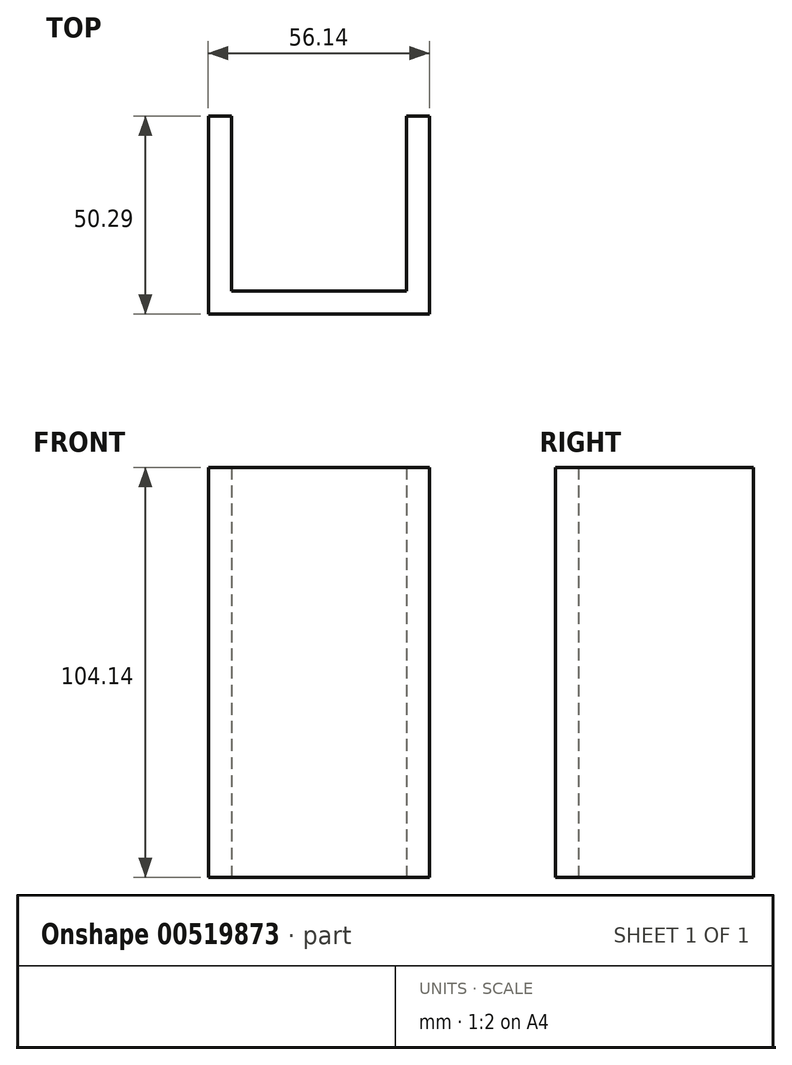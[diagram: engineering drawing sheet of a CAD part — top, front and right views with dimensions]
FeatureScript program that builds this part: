
annotation { "Feature Type Name" : "Feature", "Feature Type Description" : "" }
export const myFeature = defineFeature(function(context is Context, id is Id, definition is map)
    precondition{}
    {
        {
            var Q0;
            Q0=qCreatedBy(makeId("Top.planeOp"),FACE);
            var sketch = newSketch(context, id + "F0", { "sketchPlane" : qUnion([Q0])});
            skLineSegment(sketch, "E0", {"start": v(-14.61, -7.73) * mm, "end": v(29.84, -7.73) * mm});
            skLineSegment(sketch, "E1", {"start": v(29.84, -7.73) * mm, "end": v(29.84, 36.72) * mm});
            skLineSegment(sketch, "E2", {"start": v(29.84, 36.72) * mm, "end": v(35.68, 36.72) * mm});
            skLineSegment(sketch, "E3", {"start": v(35.68, 36.72) * mm, "end": v(35.68, -13.57) * mm});
            skLineSegment(sketch, "E4", {"start": v(35.68, -13.57) * mm, "end": v(-20.46, -13.57) * mm});
            skLineSegment(sketch, "E5", {"start": v(-14.61, -7.73) * mm, "end": v(-14.61, 36.72) * mm});
            skLineSegment(sketch, "E6", {"start": v(-14.61, 36.72) * mm, "end": v(-20.46, 36.72) * mm});
            skLineSegment(sketch, "E7", {"start": v(-20.46, 36.72) * mm, "end": v(-20.46, -13.57) * mm});
            skSolve(sketch);
        }
        {
            var Q0;
            Q0 = qSketchRegion(id + "F0", true);
            extrude(context, id + "F1", {"entities" : qUnion([Q0]), "depth" : 104.14 * mm, "offsetDistance" : 25.4 * mm});
        }
    });
